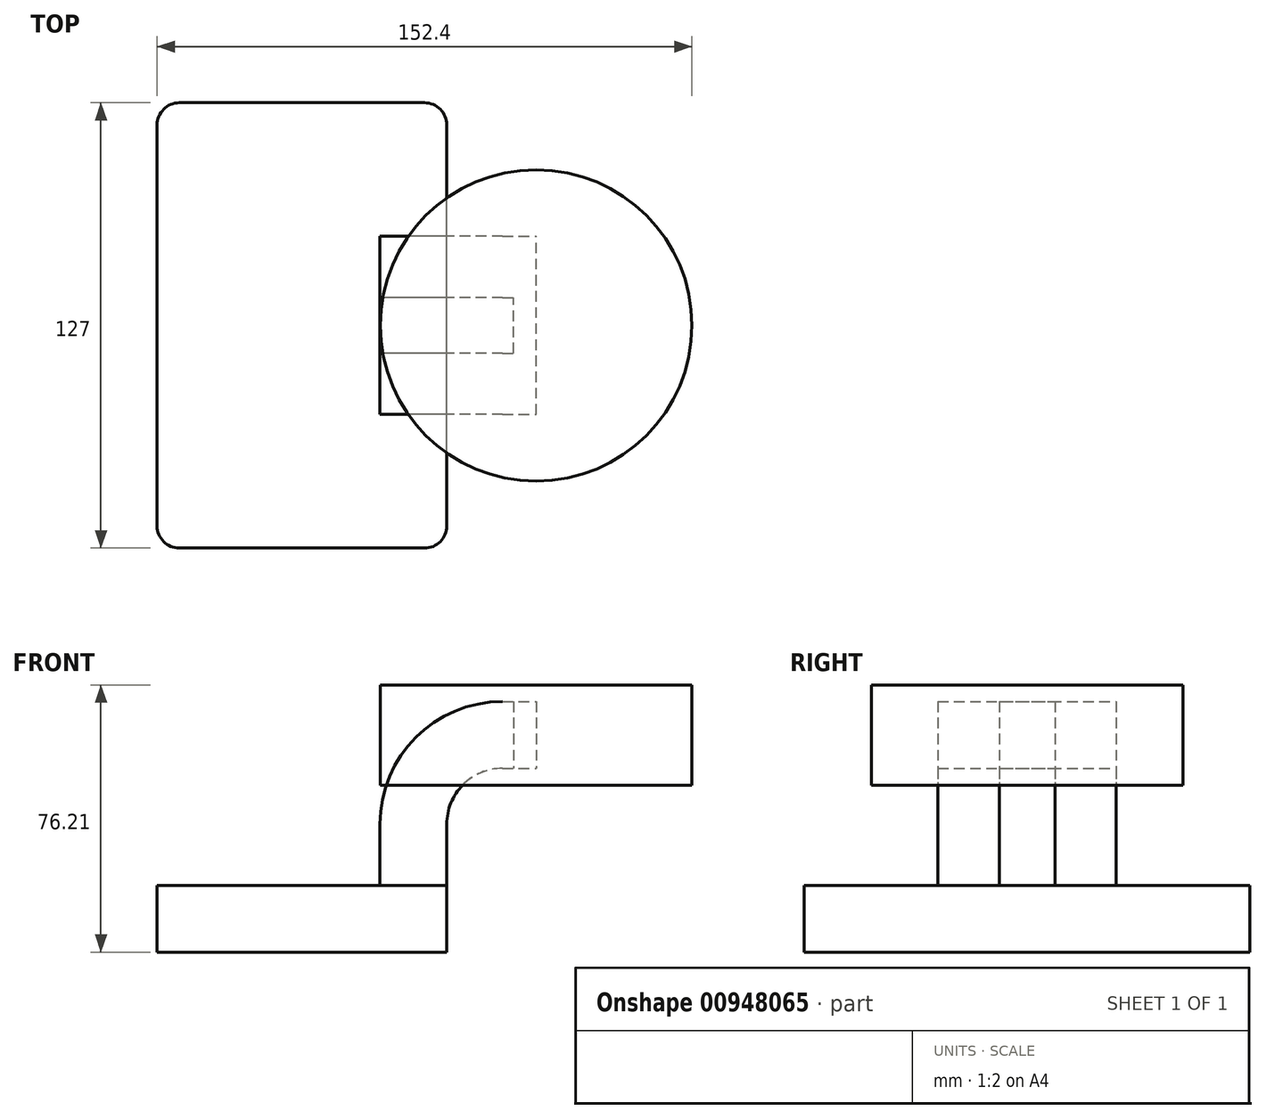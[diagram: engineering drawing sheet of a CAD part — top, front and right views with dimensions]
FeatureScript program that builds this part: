
annotation { "Feature Type Name" : "Feature", "Feature Type Description" : "" }
export const myFeature = defineFeature(function(context is Context, id is Id, definition is map)
    precondition{}
    {
        {
            var Q0;
            Q0=qCreatedBy(makeId("Front.planeOp"),FACE);
            var sketch = newSketch(context, id + "F0", { "sketchPlane" : qUnion([Q0])});
            skLineSegment(sketch, "E0.bottom", {"start": v(41.28, -9.52) * mm, "end": v(-41.27, -9.53) * mm});
            skLineSegment(sketch, "E0.top", {"start": v(41.27, 9.53) * mm, "end": v(-41.28, 9.53) * mm});
            skLineSegment(sketch, "E0.left", {"start": v(41.28, -9.52) * mm, "end": v(41.28, 9.53) * mm});
            skLineSegment(sketch, "E0.right", {"start": v(-41.27, -9.53) * mm, "end": v(-41.28, 9.53) * mm});
            skPoint(sketch, "E0.middle", {"position": v(0, 0) * mm});
            skLineSegment(sketch, "E1.bottom", {"start": v(111.12, 66.68) * mm, "end": v(60.33, 66.67) * mm});
            skLineSegment(sketch, "E1.top", {"start": v(111.12, 38.1) * mm, "end": v(60.33, 38.1) * mm});
            skLineSegment(sketch, "E1.left", {"start": v(111.12, 66.68) * mm, "end": v(111.13, 38.1) * mm});
            skLineSegment(sketch, "E1.right", {"start": v(60.33, 66.68) * mm, "end": v(60.33, 38.1) * mm});
            skPoint(sketch, "E1.middle", {"position": v(85.72, 52.39) * mm});
            skLineSegment(sketch, "E2", {"start": v(41.27, 9.53) * mm, "end": v(41.27, 27) * mm});
            skArc(sketch, "E3", {"start": v(41.27, 27) * mm, "mid": v(45.92, 38.23) * mm, "end": v(57.15, 42.88) * mm});
            skLineSegment(sketch, "E4", {"start": v(57.15, 42.88) * mm, "end": v(66.73, 42.88) * mm});
            skLineSegment(sketch, "E5.0", {"start": v(57.15, 61.93) * mm, "end": v(66.73, 61.93) * mm});
            skArc(sketch, "E5.1", {"start": v(22.23, 27) * mm, "mid": v(32.45, 51.7) * mm, "end": v(57.15, 61.93) * mm});
            skLineSegment(sketch, "E5.2", {"start": v(22.22, 9.53) * mm, "end": v(22.22, 27) * mm});
            skLineSegment(sketch, "E6", {"start": v(66.73, 66.68) * mm, "end": v(66.73, 38.1) * mm});
            skFitSpline(sketch, "E7", {"points": [v(-41.28, 9.52) * mm, v(57.15, 61.93) * mm], "startDerivative": vector(-100.81, 118.98) * mm, "endDerivative": vector(80.79, -62.91) * mm});
            skPoint(sketch, "E8.1.internal.snap0", {"position": v(32.45, 51.7) * mm});
            skSolve(sketch);
        }
        {
            var Q0;
            Q0=makeQuery(id+"F0.imprint","IMPRINT",FACE,{"disambiguationData":[TD([[makeQuery(id+"F0.imprint","IMPRINT",EDGE,{"derivedFrom":sQuery(id+"F0.wireOp",EDGE,"E0.bottom")}),-1.0]])]});
            extrude(context, id + "F1", {"entities" : qUnion([Q0]), "endBound" : BoundingType.SYMMETRIC, "depth" : 127 * mm, "offsetDistance" : 25.4 * mm});
        }
        {
            var Q0;
            {var subQ1=sQuery(id+"F0.wireOp",EDGE,"E2");Q0=makeQuery(id+"F0.imprint","IMPRINT",FACE,{"disambiguationData":[TD([[makeQuery(id+"F0.imprint","IMPRINT",EDGE,{"derivedFrom":subQ1}),1.0]])]});}
            var Q1;
            {var subQ0=sQuery(id+"F0.wireOp",EDGE,"E5.0");var subQ1=sQuery(id+"F0.wireOp",EDGE,"E1.right");var subQ2=makeQuery(id+"F0.imprint","INTERSECT",VERTEX,{"derivedFrom":[subQ1,subQ0]});Q1=makeQuery(id+"F0.imprint","IMPRINT",FACE,{"disambiguationData":[TD([[makeQuery(id+"F0.imprint","IMPRINT",EDGE,{"disambiguationData":[TD([[subQ2,-1.0]])],"derivedFrom":subQ1}),1.0]])]});}
            extrude(context, id + "F2", {"entities" : qUnion([Q0, Q1]), "endBound" : BoundingType.SYMMETRIC, "depth" : 50.8 * mm, "offsetDistance" : 25.4 * mm});
        }
        {
            var Q0;
            Q0=makeQuery(id+"F0.imprint","IMPRINT",FACE,{"disambiguationData":[TD([[makeQuery(id+"F0.imprint","IMPRINT",EDGE,{"derivedFrom":sQuery(id+"F0.wireOp",EDGE,"E5.1")}),1.0]])]});
            extrude(context, id + "F3", {"entities" : qUnion([Q0]), "endBound" : BoundingType.SYMMETRIC, "depth" : 15.88 * mm, "offsetDistance" : 25.4 * mm});
        }
        {
            var Q0;
            {var subQ4=sQuery(id+"F0.wireOp",EDGE,"E1.left");Q0=makeQuery(id+"F0.imprint","IMPRINT",FACE,{"disambiguationData":[TD([[makeQuery(id+"F0.imprint","IMPRINT",EDGE,{"derivedFrom":subQ4}),-1.0]])]});}
            var Q1;
            Q1=sQuery(id+"F0.wireOp",EDGE,"E6");
            revolve(context, id + "F4", {"surfaceOperationType" : NewSurfaceOperationType.NEW, "entities" : qUnion([Q0]), "axis" : qUnion([Q1]), "revolveType" : RevolveType.FULL});
        }
        {
            var Q0;
            Q0=makeQuery(id+"F1.opExtrude","CAP_EDGE",EDGE,{"disambiguationData":[OSD([sQuery(id+"F0.wireOp",EDGE,"E0.right")])],"isStart":false});
            var Q1;
            Q1=makeQuery(id+"F1.opExtrude","CAP_EDGE",EDGE,{"disambiguationData":[OSD([sQuery(id+"F0.wireOp",EDGE,"E0.left")])],"isStart":false});
            var Q2;
            Q2=makeQuery(id+"F1.opExtrude","CAP_EDGE",EDGE,{"disambiguationData":[OSD([sQuery(id+"F0.wireOp",EDGE,"E0.left")])],"isStart":true});
            var Q3;
            Q3=makeQuery(id+"F1.opExtrude","CAP_EDGE",EDGE,{"disambiguationData":[OSD([sQuery(id+"F0.wireOp",EDGE,"E0.right")])],"isStart":true});
            fillet(context, id + "F5", {"entities" : qUnion([Q0, Q1, Q2, Q3]), "radius" : 6.35 * mm, "tangentPropagation" : true, "allowEdgeOverflow" : false});
        }
    });
